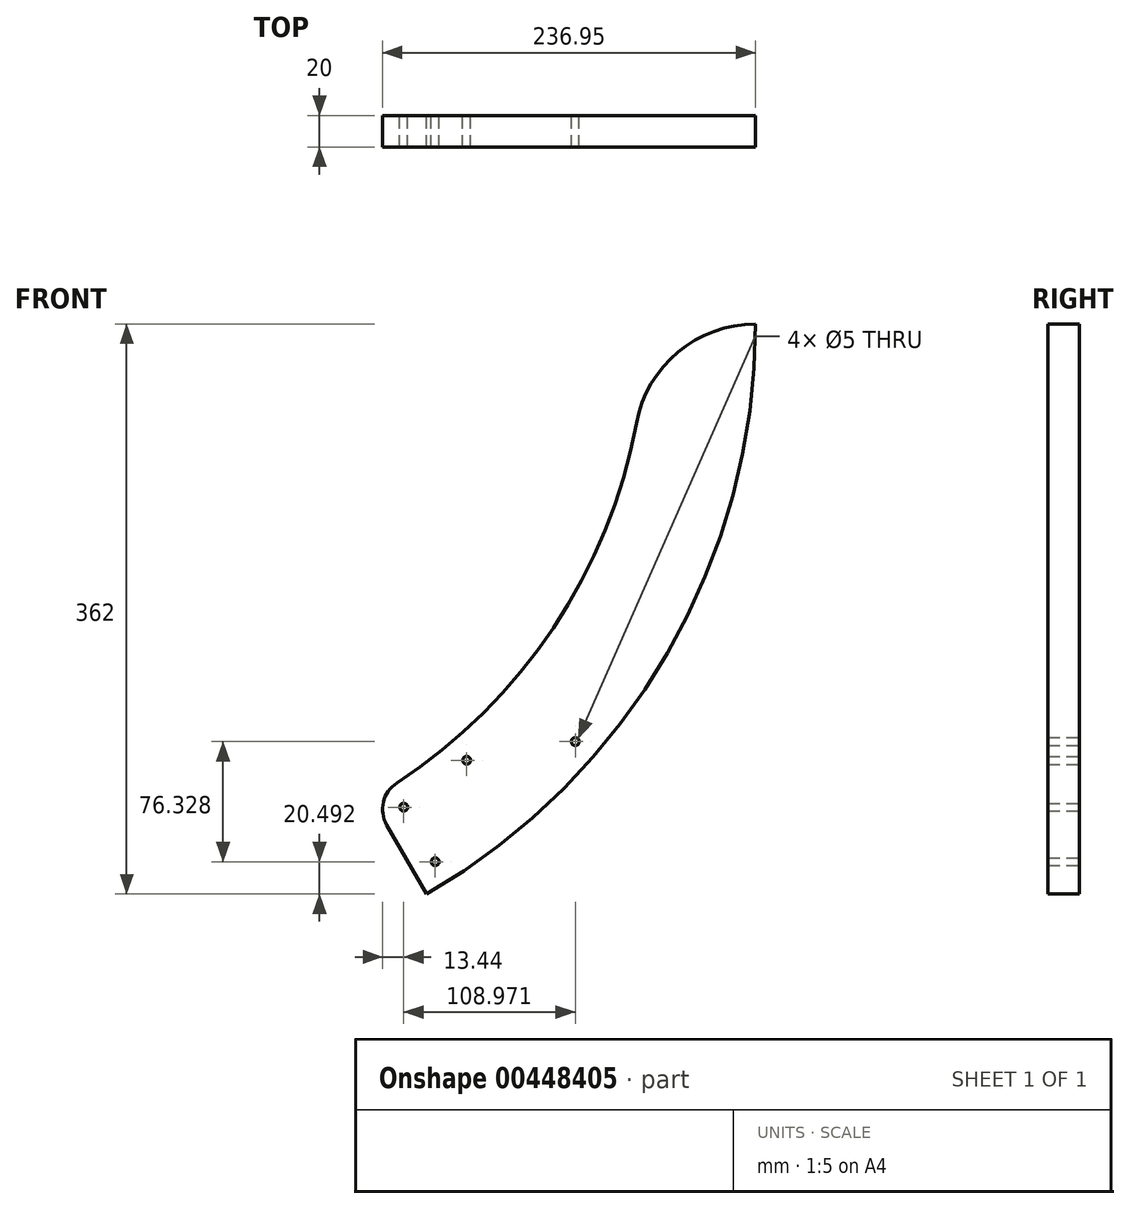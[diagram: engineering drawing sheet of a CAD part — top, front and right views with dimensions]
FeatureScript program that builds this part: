
annotation { "Feature Type Name" : "Feature", "Feature Type Description" : "" }
export const myFeature = defineFeature(function(context is Context, id is Id, definition is map)
    precondition{}
    {
        {
            var Q0;
            Q0=qCreatedBy(makeId("Front.planeOp"),FACE);
            var sketch = newSketch(context, id + "F0", { "sketchPlane" : qUnion([Q0])});
            skLineSegment(sketch, "E0", {"start": v(0, 0) * mm, "end": v(0, 418) * mm, "construction": true});
            skLineSegment(sketch, "E1", {"start": v(0, 418) * mm, "end": v(418, 418) * mm, "construction": true});
            skArc(sketch, "E2", {"start": v(418, 418) * mm, "mid": v(362, 209) * mm, "end": v(209, 56) * mm});
            skLineSegment(sketch, "E3", {"start": v(0, 418) * mm, "end": v(174, 116.62) * mm});
            skLineSegment(sketch, "E4", {"start": v(209, 56) * mm, "end": v(183.73, 99.77) * mm});
            skArc(sketch, "E5", {"start": v(183.73, 99.77) * mm, "mid": v(181.6, 114.42) * mm, "end": v(190.12, 126.53) * mm});
            skArc(sketch, "E6", {"start": v(190.12, 126.53) * mm, "mid": v(289.64, 225.1) * mm, "end": v(342.24, 354.92) * mm});
            skLineSegment(sketch, "E7", {"start": v(418, 418) * mm, "end": v(418, 340.96) * mm, "construction": true});
            skArc(sketch, "E8", {"start": v(418, 418) * mm, "mid": v(368.7, 400.17) * mm, "end": v(342.24, 354.92) * mm});
            skLineSegment(sketch, "E9", {"start": v(0, 418) * mm, "end": v(295.57, 122.43) * mm, "construction": true});
            skCircle(sketch, "E10", {"center": v(303.46, 152.82) * mm, "radius": 2.5 * mm});
            skCircle(sketch, "E11", {"center": v(234.48, 140.9) * mm, "radius": 2.5 * mm});
            skLineSegment(sketch, "E12", {"start": v(234.48, 140.9) * mm, "end": v(270.82, 147.18) * mm, "construction": true});
            skLineSegment(sketch, "E13", {"start": v(270.82, 147.18) * mm, "end": v(303.46, 152.82) * mm, "construction": true});
            skArc(sketch, "E14", {"start": v(418, 418) * mm, "mid": v(295.57, 122.43) * mm, "end": v(0, 0) * mm, "construction": true});
            skArc(sketch, "E15", {"start": v(348, 418) * mm, "mid": v(246.07, 171.93) * mm, "end": v(0, 70) * mm, "construction": true});
            skArc(sketch, "E16", {"start": v(0, 55) * mm, "mid": v(256.68, 161.32) * mm, "end": v(363, 418) * mm, "construction": true});
            skArc(sketch, "E17", {"start": v(0, 15) * mm, "mid": v(284.96, 133.04) * mm, "end": v(403, 418) * mm, "construction": true});
            skArc(sketch, "E18", {"start": v(0, 35) * mm, "mid": v(270.82, 147.18) * mm, "end": v(383, 418) * mm, "construction": true});
            skCircle(sketch, "E19", {"center": v(194.5, 111.13) * mm, "radius": 2.5 * mm});
            skLineSegment(sketch, "E20", {"start": v(0, 418) * mm, "end": v(228.36, 67.9) * mm, "construction": true});
            skCircle(sketch, "E21", {"center": v(214.5, 76.5) * mm, "radius": 2.5 * mm});
            skLineSegment(sketch, "E22", {"start": v(209, 56) * mm, "end": v(252.06, 80.86) * mm, "construction": true});
            skLineSegment(sketch, "E23", {"start": v(222, 63.5) * mm, "end": v(189.67, 119.48) * mm, "construction": true});
            skSolve(sketch);
        }
        {
            var Q0;
            Q0=qSketchRegion(id+"F0",true);
            extrude(context, id + "F1", {"entities" : qUnion([Q0]), "depth" : 20 * mm});
        }
    });
